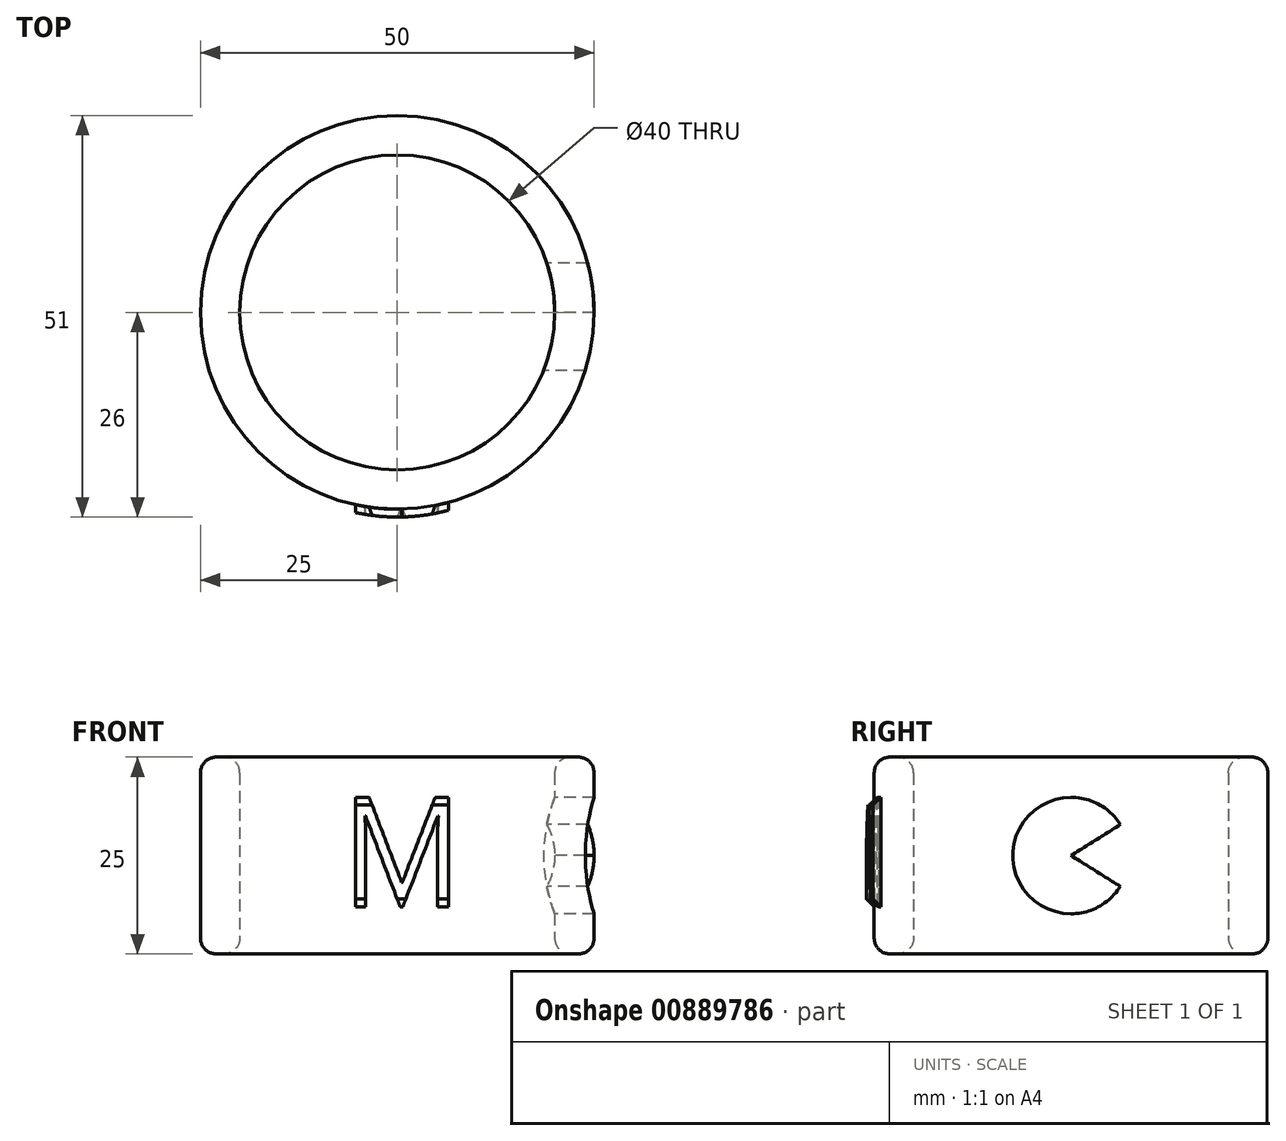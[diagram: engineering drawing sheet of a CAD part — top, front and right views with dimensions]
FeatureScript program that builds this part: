
annotation { "Feature Type Name" : "Feature", "Feature Type Description" : "" }
export const myFeature = defineFeature(function(context is Context, id is Id, definition is map)
    precondition{}
    {
        {
            var Q0;
            Q0=qCreatedBy(makeId("Top.planeOp"),FACE);
            var sketch = newSketch(context, id + "F0", { "sketchPlane" : qUnion([Q0])});
            skCircle(sketch, "E0", {"center": v(0, 0) * mm, "radius": 25 * mm});
            skCircle(sketch, "E1", {"center": v(0, 0) * mm, "radius": 20 * mm});
            skSolve(sketch);
        }
        {
            var Q0;
            Q0=makeQuery(id+"F0.imprint","IMPRINT",FACE,{"disambiguationData":[TD([[makeQuery(id+"F0.imprint","IMPRINT",EDGE,{"derivedFrom":sQuery(id+"F0.wireOp",EDGE,"E0")}),1.0]])]});
            extrude(context, id + "F1", {"entities" : qUnion([Q0]), "depth" : 25 * mm, "offsetDistance" : 25 * mm});
        }
        {
            var Q0;
            Q0=makeQuery(id+"F1.opExtrude","CAP_EDGE",EDGE,{"disambiguationData":[OSD([sQuery(id+"F0.wireOp",EDGE,"E0")])],"isStart":false});
            var Q1;
            Q1=makeQuery(id+"F1.opExtrude","CAP_EDGE",EDGE,{"disambiguationData":[OSD([sQuery(id+"F0.wireOp",EDGE,"E1")])],"isStart":false});
            var Q2;
            Q2=makeQuery(id+"F1.opExtrude","CAP_EDGE",EDGE,{"disambiguationData":[OSD([sQuery(id+"F0.wireOp",EDGE,"E0")])],"isStart":true});
            var Q3;
            Q3=makeQuery(id+"F1.opExtrude","CAP_EDGE",EDGE,{"disambiguationData":[OSD([sQuery(id+"F0.wireOp",EDGE,"E1")])],"isStart":true});
            fillet(context, id + "F2", {"entities" : qUnion([Q0, Q1, Q2, Q3]), "radius" : 2 * mm, "tangentPropagation" : true, "allowEdgeOverflow" : false});
        }
        {
            var Q0;
            Q0=qCreatedBy(makeId("Right.planeOp"),FACE);
            var sketch = newSketch(context, id + "F3", { "sketchPlane" : qUnion([Q0])});
            skArc(sketch, "E2", {"start": v(6.27, 16.42) * mm, "mid": v(-7.4, 12.5) * mm, "end": v(6.27, 8.58) * mm});
            skLineSegment(sketch, "E3", {"start": v(6.27, 16.42) * mm, "end": v(0, 12.5) * mm});
            skLineSegment(sketch, "E4", {"start": v(0, 12.5) * mm, "end": v(6.27, 8.58) * mm});
            skLineSegment(sketch, "E5.0", {"start": v(-23, 25) * mm, "end": v(23, 25) * mm});
            skLineSegment(sketch, "E6.0", {"start": v(23, 0) * mm, "end": v(-23, 0) * mm});
            skLineSegment(sketch, "E7", {"start": v(0, 0) * mm, "end": v(0, 25) * mm, "construction": true});
            skSolve(sketch);
        }
        {
            var Q0;
            Q0=makeQuery(id+"F3.imprint","IMPRINT",FACE,{"disambiguationData":[TD([[makeQuery(id+"F3.imprint","IMPRINT",EDGE,{"derivedFrom":sQuery(id+"F3.wireOp",EDGE,"E2")}),1.0]])]});
            var Q1;
            Q1=makeQuery(id+"F1.opExtrude","SWEPT_FACE",FACE,{"disambiguationData":[OSD([sQuery(id+"F0.wireOp",EDGE,"E0")])]});
            extrude(context, id + "F4", {"entities" : qUnion([Q0]), "operationType" : NewBodyOperationType.REMOVE, "endBound" : BoundingType.THROUGH_ALL, "depth" : 25 * mm, "endBoundEntityFace" : qUnion([Q1]), "hasOffset" : true, "offsetDistance" : 1 * mm});
        }
        {
            var Q0;
            Q0=qCreatedBy(makeId("Front.planeOp"),FACE);
            cPlane(context, id + "F5", {"entities" : qUnion([Q0]), "cplaneType" : CPlaneType.OFFSET, "offset" : 21.9 * mm, "width" : 150 * mm, "height" : 150 * mm});
        }
        {
            var Q0;
            Q0=qCreatedBy(id+"F5.planeOp",FACE);
            var sketch = newSketch(context, id + "F6", { "sketchPlane" : qUnion([Q0])});
            skText(sketch, "E8", { "text": "M", "fontName": "OpenSans-Regular.ttf"});
            const initialGuessF6  = {"E8": [-0.00692, 0.007, 1, 0, 0.012]};
            skSetInitialGuess(sketch, initialGuessF6);
            skSolve(sketch);
        }
        {
            var Q0;
            Q0 = qSketchRegion(id + "F6", true);
            var Q1;
            Q1=makeQuery(id+"F1.opExtrude","SWEPT_FACE",FACE,{"disambiguationData":[OSD([sQuery(id+"F0.wireOp",EDGE,"E0")])]});
            extrude(context, id + "F7", {"entities" : qUnion([Q0]), "operationType" : NewBodyOperationType.ADD, "endBound" : BoundingType.UP_TO_SURFACE, "depth" : 25 * mm, "endBoundEntityFace" : qUnion([Q1]), "hasOffset" : true, "offsetDistance" : -1 * mm});
        }
        {
            var Q0;
            Q0=makeQuery(id+"F7.boolean.opBoolean","INTERSECT",EDGE,{"derivedFrom":[makeQuery(id+"F1.opExtrude","SWEPT_FACE",FACE,{"disambiguationData":[OSD([sQuery(id+"F0.wireOp",EDGE,"E0")])]}),makeQuery(id+"F7.opExtrude","SWEPT_FACE",FACE,{"disambiguationData":[OSD([sQuery(id+"F6.wireOp",EDGE,"E8.sketch_text.stroke-10")])]})]});
            var Q1;
            Q1=makeQuery(id+"F7.boolean.opBoolean","INTERSECT",EDGE,{"derivedFrom":[makeQuery(id+"F1.opExtrude","SWEPT_FACE",FACE,{"disambiguationData":[OSD([sQuery(id+"F0.wireOp",EDGE,"E0")])]}),makeQuery(id+"F7.opExtrude","SWEPT_FACE",FACE,{"disambiguationData":[OSD([sQuery(id+"F6.wireOp",EDGE,"E8.sketch_text.stroke-6")])]})]});
            var Q2;
            Q2=makeQuery(id+"F7.boolean.opBoolean","INTERSECT",EDGE,{"derivedFrom":[makeQuery(id+"F1.opExtrude","SWEPT_FACE",FACE,{"disambiguationData":[OSD([sQuery(id+"F0.wireOp",EDGE,"E0")])]}),makeQuery(id+"F7.opExtrude","SWEPT_FACE",FACE,{"disambiguationData":[OSD([sQuery(id+"F6.wireOp",EDGE,"E8.sketch_text.stroke-12")])]})]});
            var Q3;
            Q3=makeQuery(id+"F7.boolean.opBoolean","INTERSECT",EDGE,{"derivedFrom":[makeQuery(id+"F1.opExtrude","SWEPT_FACE",FACE,{"disambiguationData":[OSD([sQuery(id+"F0.wireOp",EDGE,"E0")])]}),makeQuery(id+"F7.opExtrude","SWEPT_FACE",FACE,{"disambiguationData":[OSD([sQuery(id+"F6.wireOp",EDGE,"E8.sketch_text.stroke-4")])]})]});
            var Q4;
            Q4=makeQuery(id+"F7.boolean.opBoolean","INTERSECT",EDGE,{"derivedFrom":[makeQuery(id+"F1.opExtrude","SWEPT_FACE",FACE,{"disambiguationData":[OSD([sQuery(id+"F0.wireOp",EDGE,"E0")])]}),makeQuery(id+"F7.opExtrude","SWEPT_FACE",FACE,{"disambiguationData":[OSD([sQuery(id+"F6.wireOp",EDGE,"E8.sketch_text.stroke-17")])]})]});
            chamfer(context, id + "F8", {"entities" : qUnion([Q0, Q1, Q2, Q3, Q4]), "width" : 1 * mm, "tangentPropagation" : true});
        }
    });
